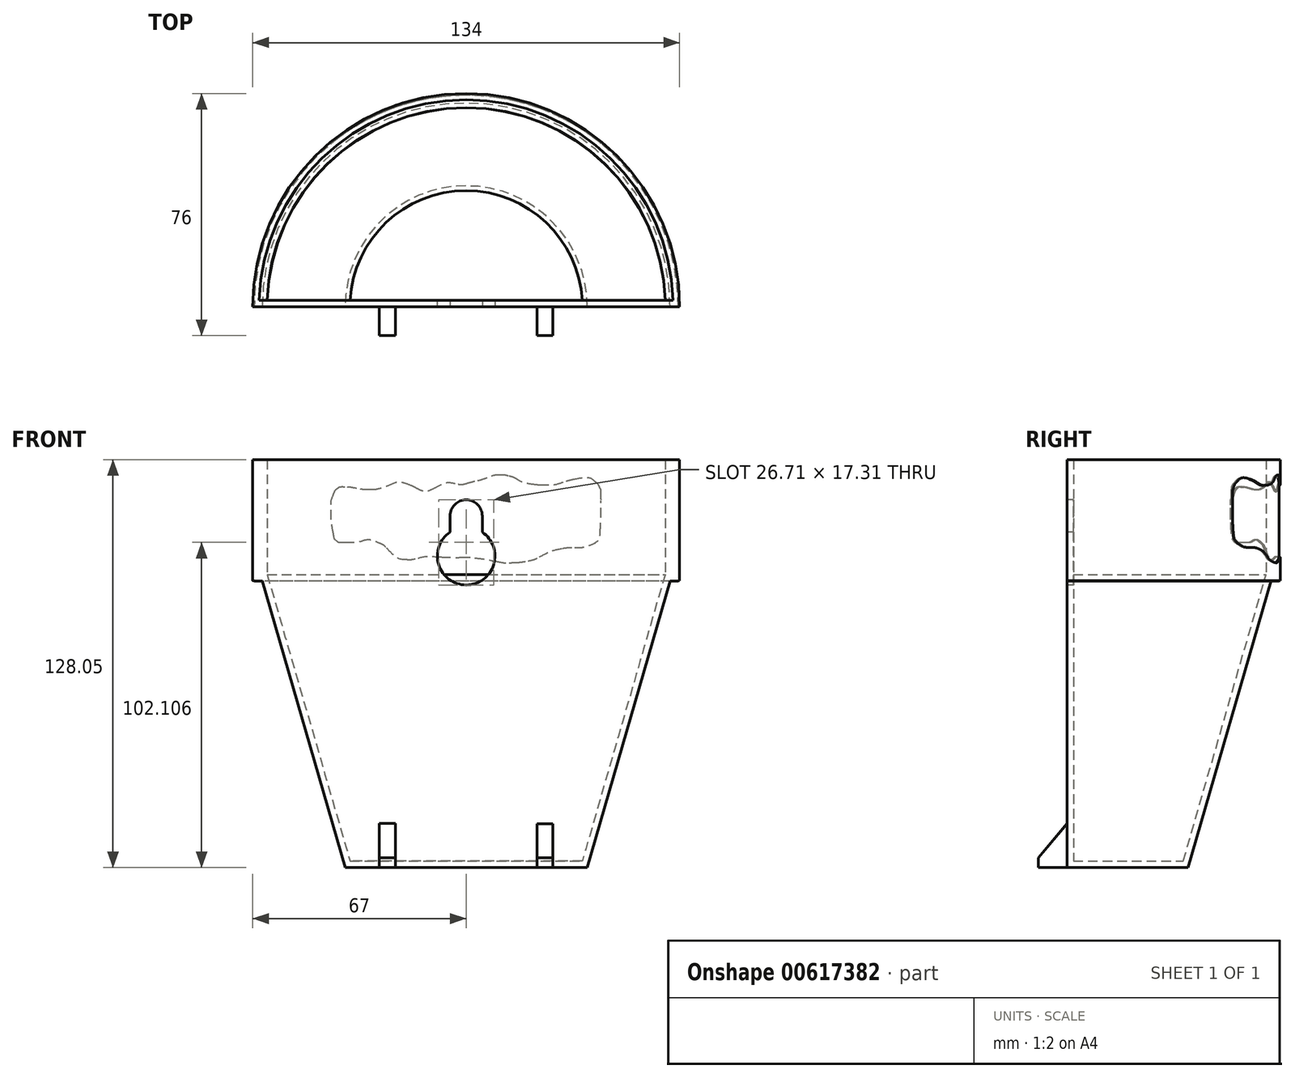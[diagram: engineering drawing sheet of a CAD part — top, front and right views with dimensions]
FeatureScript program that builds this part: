
annotation { "Feature Type Name" : "Feature", "Feature Type Description" : "" }
export const myFeature = defineFeature(function(context is Context, id is Id, definition is map)
    precondition{}
    {
        {
            var Q0;
            Q0=qCreatedBy(makeId("Front.planeOp"),FACE);
            var sketch = newSketch(context, id + "F0", { "sketchPlane" : qUnion([Q0])});
            skLineSegment(sketch, "E0", {"start": v(0, 56.42) * mm, "end": v(-67, 56.42) * mm});
            skLineSegment(sketch, "E1", {"start": v(-67, 56.42) * mm, "end": v(-67, 18.42) * mm});
            skLineSegment(sketch, "E2", {"start": v(0, -71.58) * mm, "end": v(-38, -71.58) * mm});
            skLineSegment(sketch, "E3", {"start": v(-67, 18.42) * mm, "end": v(-64, 18.42) * mm});
            skLineSegment(sketch, "E4", {"start": v(0, 56.42) * mm, "end": v(0, -71.58) * mm});
            skLineSegment(sketch, "E5", {"start": v(-64, 18.42) * mm, "end": v(-38, -71.58) * mm});
            skLineSegment(sketch, "E6.MirrorCS", {"start": v(0, 56.42) * mm, "end": v(67, 56.42) * mm});
            skLineSegment(sketch, "E7.MirrorCS", {"start": v(67, 56.42) * mm, "end": v(67, 18.42) * mm});
            skLineSegment(sketch, "E8.MirrorCS", {"start": v(67, 18.42) * mm, "end": v(64, 18.42) * mm});
            skLineSegment(sketch, "E9.MirrorCS", {"start": v(64, 18.42) * mm, "end": v(38, -71.58) * mm});
            skLineSegment(sketch, "E10.MirrorCS", {"start": v(0, -71.58) * mm, "end": v(38, -71.58) * mm});
            skSolve(sketch);
        }
        {
            var Q0;
            {var subQ0=sQuery(id+"F0.wireOp",EDGE,"E3");Q0=makeQuery(id+"F0.imprint","IMPRINT",FACE,{"disambiguationData":[TD([[makeQuery(id+"F0.imprint","IMPRINT",EDGE,{"derivedFrom":subQ0}),1.0]])]});}
            var Q1;
            {var subQ1=sQuery(id+"F0.wireOp",EDGE,"E0");Q1=makeQuery(id+"F0.imprint","IMPRINT",FACE,{"disambiguationData":[TD([[makeQuery(id+"F0.imprint","IMPRINT",EDGE,{"derivedFrom":subQ1}),1.0]])]});}
            var Q2;
            Q2=makeQuery(id+"F0.imprint","IMPRINT",FACE,{"disambiguationData":[TD([[makeQuery(id+"F0.imprint","IMPRINT",EDGE,{"derivedFrom":sQuery(id+"F0.wireOp",EDGE,"Kfnrekvc-ZjTY-c2iQ-cK4z-hKnBe4uEAVNk")}),1.0]])]});
            var Q3;
            Q3=sQuery(id+"F0.wireOp",EDGE,"E4");
            revolve(context, id + "F1", {"entities" : qUnion([Q0, Q1, Q2]), "axis" : qUnion([Q3]), "revolveType" : RevolveType.ONE_DIRECTION, "angle" : 180 * degree});
        }
        {
            var Q0;
            Q0=makeQuery(id+"FK2OT3XlAi37Aaq_1.splitOp","SPLIT",FACE,{"derivedFrom":makeQuery(id+"F1.opRevolve","SWEPT_FACE",FACE,{"disambiguationData":[OSD([sQuery(id+"F0.wireOp",EDGE,"E0")])]}),"isFromBackBody":true});
            shell(context, id + "F2", {"entities" : qUnion([Q0]), "thickness" : 2 * mm});
        }
        {
            var Q0;
            Q0=qCreatedBy(makeId("Front.planeOp"),FACE);
            var sketch = newSketch(context, id + "F3", { "sketchPlane" : qUnion([Q0])});
            skPoint(sketch, "E11.middle", {"position": v(0, -64.08) * mm});
            skLineSegment(sketch, "E12.bottom", {"start": v(-27.21, -56.57) * mm, "end": v(-22.21, -56.57) * mm});
            skLineSegment(sketch, "E12.top", {"start": v(-27.21, -71.57) * mm, "end": v(-22.21, -71.57) * mm});
            skLineSegment(sketch, "E12.left", {"start": v(-27.21, -56.57) * mm, "end": v(-27.21, -71.57) * mm});
            skLineSegment(sketch, "E12.right", {"start": v(-22.21, -56.57) * mm, "end": v(-22.21, -71.57) * mm});
            skPoint(sketch, "E12.middle", {"position": v(-24.71, -64.07) * mm});
            skLineSegment(sketch, "E13.bottom", {"start": v(22.21, -56.63) * mm, "end": v(27.21, -56.63) * mm});
            skLineSegment(sketch, "E13.top", {"start": v(22.21, -71.63) * mm, "end": v(27.21, -71.63) * mm});
            skLineSegment(sketch, "E13.left", {"start": v(22.21, -56.63) * mm, "end": v(22.21, -71.63) * mm});
            skLineSegment(sketch, "E13.right", {"start": v(27.21, -56.63) * mm, "end": v(27.21, -71.63) * mm});
            skPoint(sketch, "E13.middle", {"position": v(24.71, -64.13) * mm});
            skLineSegment(sketch, "E14", {"start": v(0, -71.68) * mm, "end": v(-22.21, -71.57) * mm, "construction": true});
            skLineSegment(sketch, "E15", {"start": v(0, -71.68) * mm, "end": v(22.21, -71.63) * mm, "construction": true});
            skSolve(sketch);
        }
        {
            var Q0;
            Q0=qSketchRegion(id+"F3",true);
            extrude(context, id + "F4", {"entities" : qUnion([Q0]), "operationType" : NewBodyOperationType.ADD, "depth" : 9 * mm});
        }
        {
            var Q0;
            Q0=qCreatedBy(makeId("Front.planeOp"),FACE);
            var sketch = newSketch(context, id + "F5", { "sketchPlane" : qUnion([Q0])});
            skCircle(sketch, "E16", {"center": v(0, 26.17) * mm, "radius": 9.05 * mm});
            skArc(sketch, "E17", {"start": v(5.05, 38.78) * mm, "mid": v(0.02, 43.83) * mm, "end": v(-5.05, 38.81) * mm});
            skLineSegment(sketch, "E18", {"start": v(-5.05, 38.81) * mm, "end": v(-5.05, 33.68) * mm});
            skLineSegment(sketch, "E19", {"start": v(5.05, 38.78) * mm, "end": v(5.05, 33.68) * mm});
            skSolve(sketch);
        }
        {
            var Q0;
            {var subQ0=sQuery(id+"F5.wireOp",EDGE,"E16");var subQ1=sQuery(id+"F5.wireOp",EDGE,"mXHq6PA0-CqQh-Lv1D-GdnR-uttjTBgCqYAd");var subQ2=makeQuery(id+"F5.imprint","INTERSECT",VERTEX,{"disambiguationData":[OD(0.0)],"derivedFrom":[subQ1,subQ0]});Q0=makeQuery(id+"F5.imprint","IMPRINT",FACE,{"disambiguationData":[TD([[makeQuery(id+"F5.imprint","IMPRINT",EDGE,{"disambiguationData":[TD([[subQ2,1.0]])],"derivedFrom":subQ1}),1.0]])]});}
            var Q1;
            {var subQ0=sQuery(id+"F5.wireOp",EDGE,"E16");var subQ1=sQuery(id+"F5.wireOp",EDGE,"mXHq6PA0-CqQh-Lv1D-GdnR-uttjTBgCqYAd");var subQ2=makeQuery(id+"F5.imprint","INTERSECT",VERTEX,{"disambiguationData":[OD(0.0)],"derivedFrom":[subQ1,subQ0]});Q1=makeQuery(id+"F5.imprint","IMPRINT",FACE,{"disambiguationData":[TD([[makeQuery(id+"F5.imprint","IMPRINT",EDGE,{"disambiguationData":[TD([[subQ2,-1.0]])],"derivedFrom":subQ1}),-1.0]])]});}
            var Q2;
            {var subQ0=sQuery(id+"F5.wireOp",EDGE,"E16");var subQ1=sQuery(id+"F5.wireOp",EDGE,"mXHq6PA0-CqQh-Lv1D-GdnR-uttjTBgCqYAd");var subQ2=makeQuery(id+"F5.imprint","INTERSECT",VERTEX,{"disambiguationData":[OD(0.0)],"derivedFrom":[subQ1,subQ0]});Q2=makeQuery(id+"F5.imprint","IMPRINT",FACE,{"disambiguationData":[TD([[makeQuery(id+"F5.imprint","IMPRINT",EDGE,{"disambiguationData":[TD([[subQ2,-1.0]])],"derivedFrom":subQ1}),1.0]])]});}
            var Q3;
            Q3=makeQuery(id+"F5.imprint","IMPRINT",FACE,{"disambiguationData":[TD([[makeQuery(id+"F5.imprint","IMPRINT",EDGE,{"derivedFrom":sQuery(id+"F5.wireOp",EDGE,"E17")}),1.0]])]});
            var Q4;
            {var subQ0=sQuery(id+"F5.wireOp",EDGE,"E16");var subQ1=makeQuery(id+"F5.imprint","INTERSECT",VERTEX,{"derivedFrom":[subQ0,sQuery(id+"F5.wireOp",EDGE,"E18")]});Q4=makeQuery(id+"F5.imprint","IMPRINT",FACE,{"disambiguationData":[TD([[makeQuery(id+"F5.imprint","IMPRINT",EDGE,{"disambiguationData":[TD([[subQ1,1.0]])],"derivedFrom":subQ0}),1.0]])]});}
            var Q5;
            Q5=sQuery(id+"F5.wireOp",EDGE,"mXHq6PA0-CqQh-Lv1D-GdnR-uttjTBgCqYAd");
            var Q6;
            Q6=sQuery(id+"F5.wireOp",EDGE,"E16");
            extrude(context, id + "F6", {"entities" : qUnion([Q0, Q1, Q2, Q3, Q4]), "operationType" : NewBodyOperationType.REMOVE, "surfaceEntities" : qUnion([Q5, Q6]), "oppositeDirection" : true, "depth" : 10 * mm, "offsetDistance" : 25 * mm});
        }
        {
            var Q0;
            Q0=makeQuery(id+"F4.opExtrude","CAP_EDGE",EDGE,{"disambiguationData":[OSD([sQuery(id+"F3.wireOp",EDGE,"E11.bottom")])],"isStart":false});
            var Q1;
            Q1=makeQuery(id+"F4.opExtrude","CAP_EDGE",EDGE,{"disambiguationData":[OSD([sQuery(id+"F3.wireOp",EDGE,"E12.bottom")])],"isStart":false});
            var Q2;
            Q2=makeQuery(id+"F4.opExtrude","CAP_EDGE",EDGE,{"disambiguationData":[OSD([sQuery(id+"F3.wireOp",EDGE,"E13.bottom")])],"isStart":false});
            chamfer(context, id + "F7", {"entities" : qUnion([Q0, Q1, Q2]), "chamferType" : ChamferType.OFFSET_ANGLE, "width" : 10 * mm, "oppositeDirection" : false, "angle" : 50 * degree, "tangentPropagation" : true});
        }
        {
            var Q0;
            Q0=makeQuery(id+"F2.opShell","OFFSET_FACE",FACE,{"disambiguationData":[OSD([sQuery(id+"F0.wireOp",EDGE,"E0"),sQuery(id+"F0.wireOp",EDGE,"E1"),sQuery(id+"F0.wireOp",EDGE,"E2"),sQuery(id+"F0.wireOp",EDGE,"E3"),sQuery(id+"F0.wireOp",EDGE,"E4"),sQuery(id+"F0.wireOp",EDGE,"E5")])]});
            cPlane(context, id + "F8", {"entities" : qUnion([Q0]), "cplaneType" : CPlaneType.OFFSET, "offset" : 66.8 * mm, "width" : 150 * mm, "height" : 150 * mm});
        }
        {
            var Q0;
            Q0=makeQuery(id+"F1.opRevolve","SWEPT_FACE",FACE,{"disambiguationData":[OSD([sQuery(id+"F0.wireOp",EDGE,"E0")])]});
            var sketch = newSketch(context, id + "F9", { "sketchPlane" : qUnion([Q0])});
            skCircle(sketch, "E20", {"center": v(0, 0) * mm, "radius": 67.75 * mm});
            skCircle(sketch, "E21", {"center": v(0, 0) * mm, "radius": 91 * mm});
            skSolve(sketch);
        }
        {
            var Q0;
            Q0=qSketchRegion(id+"F9",true);
            extrude(context, id + "F10", {"entities" : qUnion([Q0]), "operationType" : NewBodyOperationType.REMOVE, "oppositeDirection" : true, "depth" : 124 * mm});
        }
        {
            var Q0;
            Q0=qCreatedBy(id+"F8.planeOp",FACE);
            var sketch = newSketch(context, id + "F11", { "sketchPlane" : qUnion([Q0])});
            skFitSpline(sketch, "E22", {"points": [v(-14.21, 60.71) * mm, v(-15.23, 60.8) * mm, v(-17.15, 61.07) * mm, v(-17.98, 61.24) * mm]});
            skFitSpline(sketch, "E23", {"points": [v(-17.98, 61.24) * mm, v(-19.27, 61.5) * mm, v(-20.2, 61.84) * mm, v(-21.41, 62.47) * mm]});
            skFitSpline(sketch, "E24", {"points": [v(-21.41, 62.47) * mm, v(-24.2, 63.93) * mm, v(-26.13, 64.66) * mm, v(-28.48, 65.15) * mm]});
            skFitSpline(sketch, "E25", {"points": [v(-28.48, 65.15) * mm, v(-29.29, 65.32) * mm, v(-30, 65.37) * mm, v(-32.2, 65.43) * mm]});
            skFitSpline(sketch, "E26", {"points": [v(-32.2, 65.43) * mm, v(-35.22, 65.52) * mm, v(-35.76, 65.6) * mm, v(-36.93, 66.16) * mm]});
            skFitSpline(sketch, "E27", {"points": [v(-36.93, 66.16) * mm, v(-38.77, 67.04) * mm, v(-39.83, 68.44) * mm, v(-40.02, 70.25) * mm]});
            skFitSpline(sketch, "E28", {"points": [v(-40.02, 70.25) * mm, v(-40.16, 71.57) * mm, v(-40.28, 76.7) * mm, v(-40.26, 80.14) * mm]});
            skFitSpline(sketch, "E29", {"points": [v(-39.96, 84.14) * mm, v(-39.6, 85.02) * mm, v(-39.23, 85.55) * mm, v(-38.6, 86.04) * mm]});
            skFitSpline(sketch, "E30", {"points": [v(-38.6, 86.04) * mm, v(-37.32, 87.06) * mm, v(-35.24, 87.34) * mm, v(-32.5, 86.87) * mm]});
            skFitSpline(sketch, "E31", {"points": [v(-32.5, 86.87) * mm, v(-31.47, 86.7) * mm, v(-30.34, 86.4) * mm, v(-28.67, 85.86) * mm]});
            skFitSpline(sketch, "E32", {"points": [v(-28.67, 85.86) * mm, v(-26.48, 85.16) * mm, v(-25.24, 84.96) * mm, v(-23.15, 84.96) * mm]});
            skFitSpline(sketch, "E33", {"points": [v(-23.15, 84.96) * mm, v(-22.35, 84.96) * mm, v(-21.18, 85.03) * mm, v(-20.54, 85.12) * mm]});
            skFitSpline(sketch, "E34", {"points": [v(-20.54, 85.12) * mm, v(-18.34, 85.42) * mm, v(-15.77, 86.13) * mm, v(-14.88, 86.67) * mm]});
            skFitSpline(sketch, "E35", {"points": [v(-14.88, 86.67) * mm, v(-14.07, 87.17) * mm, v(-12.87, 87.67) * mm, v(-11.9, 87.91) * mm]});
            skFitSpline(sketch, "E36", {"points": [v(-11.9, 87.91) * mm, v(-11.18, 88.1) * mm, v(-10.77, 88.13) * mm, v(-9.58, 88.13) * mm]});
            skFitSpline(sketch, "E37", {"points": [v(-9.58, 88.13) * mm, v(-7.91, 88.13) * mm, v(-7.18, 87.99) * mm, v(-5.29, 87.27) * mm]});
            skFitSpline(sketch, "E38", {"points": [v(-5.29, 87.27) * mm, v(-3.99, 86.78) * mm, v(-2.9, 86.45) * mm, v(-1.6, 86.14) * mm]});
            skFitSpline(sketch, "E39", {"points": [v(-1.6, 86.14) * mm, v(-1.1, 86.03) * mm, v(-0.13, 85.78) * mm, v(0.55, 85.59) * mm]});
            skFitSpline(sketch, "E40", {"points": [v(0.55, 85.59) * mm, v(2.03, 85.17) * mm, v(2.79, 85.14) * mm, v(4.3, 85.4) * mm]});
            skFitSpline(sketch, "E41", {"points": [v(4.3, 85.4) * mm, v(6.34, 85.76) * mm, v(7.65, 85.52) * mm, v(10.1, 84.34) * mm]});
            skFitSpline(sketch, "E42", {"points": [v(10.1, 84.34) * mm, v(12.42, 83.22) * mm, v(13.55, 82.94) * mm, v(14.56, 83.25) * mm]});
            skFitSpline(sketch, "E43", {"points": [v(14.56, 83.25) * mm, v(14.85, 83.34) * mm, v(15.6, 83.69) * mm, v(16.21, 84.03) * mm]});
            skFitSpline(sketch, "E44", {"points": [v(16.21, 84.03) * mm, v(16.83, 84.37) * mm, v(17.63, 84.77) * mm, v(17.97, 84.9) * mm]});
            skFitSpline(sketch, "E45", {"points": [v(17.97, 84.9) * mm, v(19, 85.32) * mm, v(21.27, 85.96) * mm, v(22.8, 85.75) * mm]});
            skFitSpline(sketch, "E46", {"points": [v(22.8, 85.75) * mm, v(25.09, 84.74) * mm, v(26.57, 84.16) * mm, v(27.89, 83.82) * mm]});
            skFitSpline(sketch, "E47", {"points": [v(27.89, 83.82) * mm, v(28.82, 83.6) * mm, v(29.1, 83.56) * mm, v(30.58, 83.57) * mm]});
            skFitSpline(sketch, "E48", {"points": [v(30.58, 83.57) * mm, v(32.1, 83.57) * mm, v(32.41, 83.6) * mm, v(34.6, 84) * mm]});
            skFitSpline(sketch, "E49", {"points": [v(34.6, 84) * mm, v(36.58, 84.35) * mm, v(37.14, 84.42) * mm, v(38.19, 84.42) * mm]});
            skFitSpline(sketch, "E50", {"points": [v(38.19, 84.42) * mm, v(39.58, 84.42) * mm, v(39.98, 84.31) * mm, v(40.62, 83.8) * mm]});
            skFitSpline(sketch, "E51", {"points": [v(40.62, 83.8) * mm, v(41.14, 83.38) * mm, v(41.5, 82.8) * mm, v(41.88, 81.74) * mm]});
            skFitSpline(sketch, "E52", {"points": [v(41.88, 81.74) * mm, v(42.44, 80.2) * mm, v(42.49, 79.85) * mm, v(42.49, 77.2) * mm]});
            skFitSpline(sketch, "E53", {"points": [v(42.49, 77.2) * mm, v(42.48, 74.69) * mm, v(42.34, 72.96) * mm, v(41.92, 70.56) * mm]});
            skFitSpline(sketch, "E54", {"points": [v(41.92, 70.56) * mm, v(41.56, 68.48) * mm, v(41.46, 68.19) * mm, v(40.86, 67.68) * mm]});
            skFitSpline(sketch, "E55", {"points": [v(40.86, 67.68) * mm, v(40.27, 67.18) * mm, v(39.77, 67.05) * mm, v(38.23, 67.05) * mm]});
            skFitSpline(sketch, "E56", {"points": [v(38.23, 67.05) * mm, v(35.56, 67.04) * mm, v(34.05, 67.16) * mm, v(33.1, 67.44) * mm]});
            skFitSpline(sketch, "E57", {"points": [v(33.1, 67.44) * mm, v(31.4, 67.95) * mm, v(30.14, 67.86) * mm, v(28.22, 67.1) * mm]});
            skFitSpline(sketch, "E58", {"points": [v(28.22, 67.1) * mm, v(26.75, 66.51) * mm, v(26.28, 66.21) * mm, v(25.37, 65.28) * mm]});
            skFitSpline(sketch, "E59", {"points": [v(25.37, 65.28) * mm, v(23.19, 63.06) * mm, v(21.33, 61.94) * mm, v(19.52, 61.74) * mm]});
            skFitSpline(sketch, "E60", {"points": [v(19.52, 61.74) * mm, v(18.5, 61.63) * mm, v(17.41, 61.74) * mm, v(15.77, 62.11) * mm]});
            skFitSpline(sketch, "E61", {"points": [v(15.77, 62.11) * mm, v(13.66, 62.6) * mm, v(12.37, 62.66) * mm, v(8.71, 62.47) * mm]});
            skFitSpline(sketch, "E62", {"points": [v(8.71, 62.47) * mm, v(6.82, 62.37) * mm, v(4.44, 62.32) * mm, v(2.66, 62.33) * mm]});
            skFitSpline(sketch, "E63", {"points": [v(2.66, 62.33) * mm, v(0.28, 62.35) * mm, v(-0.53, 62.32) * mm, v(-1.6, 62.18) * mm]});
            skFitSpline(sketch, "E64", {"points": [v(-1.6, 62.18) * mm, v(-3.69, 61.9) * mm, v(-5.8, 61.56) * mm, v(-8.26, 61.08) * mm]});
            skFitSpline(sketch, "E65", {"points": [v(-8.26, 61.08) * mm, v(-10.46, 60.66) * mm, v(-10.6, 60.65) * mm, v(-12.2, 60.67) * mm]});
            skFitSpline(sketch, "E66", {"points": [v(-12.2, 60.67) * mm, v(-13.1, 60.68) * mm, v(-14, 60.7) * mm, v(-14.21, 60.71) * mm]});
            skLineSegment(sketch, "E67", {"start": v(-40.26, 80.14) * mm, "end": v(-40.23, 83.46) * mm});
            skLineSegment(sketch, "E68", {"start": v(-40.23, 83.46) * mm, "end": v(-39.96, 84.14) * mm});
            skLineSegment(sketch, "E69", {"start": v(-39.96, 84.14) * mm, "end": v(-40.26, 80.14) * mm});
            skFitSpline(sketch, "E70", {"points": [v(-15.59, 24.15) * mm, v(-16.63, 24.24) * mm, v(-18.6, 24.5) * mm, v(-19.44, 24.68) * mm]});
            skFitSpline(sketch, "E71", {"points": [v(-19.44, 24.68) * mm, v(-20.76, 24.94) * mm, v(-21.72, 25.28) * mm, v(-22.96, 25.91) * mm]});
            skFitSpline(sketch, "E72", {"points": [v(-22.96, 25.91) * mm, v(-25.81, 27.37) * mm, v(-27.79, 28.1) * mm, v(-30.2, 28.6) * mm]});
            skFitSpline(sketch, "E73", {"points": [v(-30.2, 28.6) * mm, v(-31.02, 28.76) * mm, v(-31.76, 28.81) * mm, v(-34.01, 28.87) * mm]});
            skFitSpline(sketch, "E74", {"points": [v(-34.01, 28.87) * mm, v(-37.1, 28.96) * mm, v(-37.65, 29.04) * mm, v(-38.85, 29.6) * mm]});
            skFitSpline(sketch, "E75", {"points": [v(-38.85, 29.6) * mm, v(-40.73, 30.48) * mm, v(-41.82, 31.88) * mm, v(-42.02, 33.69) * mm]});
            skFitSpline(sketch, "E76", {"points": [v(-42.02, 33.69) * mm, v(-42.16, 35) * mm, v(-42.29, 40.13) * mm, v(-42.26, 43.57) * mm]});
            skFitSpline(sketch, "E77", {"points": [v(-41.95, 47.57) * mm, v(-41.59, 48.46) * mm, v(-41.2, 48.98) * mm, v(-40.57, 49.47) * mm]});
            skFitSpline(sketch, "E78", {"points": [v(-40.57, 49.47) * mm, v(-39.25, 50.5) * mm, v(-37.12, 50.77) * mm, v(-34.3, 50.3) * mm]});
            skFitSpline(sketch, "E79", {"points": [v(-34.3, 50.3) * mm, v(-33.26, 50.13) * mm, v(-32.1, 49.83) * mm, v(-30.4, 49.3) * mm]});
            skFitSpline(sketch, "E80", {"points": [v(-30.4, 49.3) * mm, v(-28.15, 48.6) * mm, v(-26.88, 48.4) * mm, v(-24.74, 48.4) * mm]});
            skFitSpline(sketch, "E81", {"points": [v(-24.74, 48.4) * mm, v(-23.91, 48.4) * mm, v(-22.72, 48.47) * mm, v(-22.06, 48.56) * mm]});
            skFitSpline(sketch, "E82", {"points": [v(-22.06, 48.56) * mm, v(-19.81, 48.86) * mm, v(-17.18, 49.56) * mm, v(-16.26, 50.1) * mm]});
            skFitSpline(sketch, "E83", {"points": [v(-16.26, 50.1) * mm, v(-15.44, 50.6) * mm, v(-14.2, 51.1) * mm, v(-13.21, 51.35) * mm]});
            skFitSpline(sketch, "E84", {"points": [v(-13.21, 51.35) * mm, v(-12.48, 51.53) * mm, v(-12.06, 51.57) * mm, v(-10.84, 51.57) * mm]});
            skFitSpline(sketch, "E85", {"points": [v(-10.84, 51.57) * mm, v(-9.13, 51.57) * mm, v(-8.38, 51.42) * mm, v(-6.44, 50.7) * mm]});
            skFitSpline(sketch, "E86", {"points": [v(-6.44, 50.7) * mm, v(-5.11, 50.21) * mm, v(-4, 49.88) * mm, v(-2.67, 49.58) * mm]});
            skFitSpline(sketch, "E87", {"points": [v(-2.67, 49.58) * mm, v(-2.15, 49.46) * mm, v(-1.16, 49.21) * mm, v(-0.46, 49.02) * mm]});
            skFitSpline(sketch, "E88", {"points": [v(-0.46, 49.02) * mm, v(1.05, 48.61) * mm, v(1.82, 48.57) * mm, v(3.38, 48.84) * mm]});
            skFitSpline(sketch, "E89", {"points": [v(3.38, 48.84) * mm, v(5.46, 49.2) * mm, v(6.8, 48.96) * mm, v(9.3, 47.78) * mm]});
            skFitSpline(sketch, "E90", {"points": [v(9.3, 47.78) * mm, v(11.69, 46.66) * mm, v(12.85, 46.38) * mm, v(13.88, 46.69) * mm]});
            skFitSpline(sketch, "E91", {"points": [v(13.88, 46.69) * mm, v(14.18, 46.77) * mm, v(14.94, 47.12) * mm, v(15.57, 47.47) * mm]});
            skFitSpline(sketch, "E92", {"points": [v(15.57, 47.47) * mm, v(16.21, 47.8) * mm, v(17.02, 48.2) * mm, v(17.38, 48.34) * mm]});
            skFitSpline(sketch, "E93", {"points": [v(17.38, 48.34) * mm, v(18.43, 48.76) * mm, v(20.75, 49.4) * mm, v(22.33, 49.19) * mm]});
            skFitSpline(sketch, "E94", {"points": [v(22.33, 49.19) * mm, v(24.66, 48.17) * mm, v(26.18, 47.6) * mm, v(27.53, 47.26) * mm]});
            skFitSpline(sketch, "E95", {"points": [v(27.53, 47.26) * mm, v(28.48, 47.03) * mm, v(28.77, 47) * mm, v(30.29, 47) * mm]});
            skFitSpline(sketch, "E96", {"points": [v(30.29, 47) * mm, v(31.85, 47) * mm, v(32.17, 47.04) * mm, v(34.4, 47.43) * mm]});
            skFitSpline(sketch, "E97", {"points": [v(34.4, 47.43) * mm, v(36.44, 47.79) * mm, v(37, 47.85) * mm, v(38.08, 47.85) * mm]});
            skFitSpline(sketch, "E98", {"points": [v(38.08, 47.85) * mm, v(39.5, 47.85) * mm, v(39.91, 47.75) * mm, v(40.57, 47.23) * mm]});
            skFitSpline(sketch, "E99", {"points": [v(40.57, 47.23) * mm, v(41.1, 46.81) * mm, v(41.47, 46.23) * mm, v(41.86, 45.17) * mm]});
            skFitSpline(sketch, "E100", {"points": [v(41.86, 45.17) * mm, v(42.44, 43.64) * mm, v(42.49, 43.29) * mm, v(42.48, 40.64) * mm]});
            skFitSpline(sketch, "E101", {"points": [v(42.48, 40.64) * mm, v(42.48, 38.12) * mm, v(42.33, 36.4) * mm, v(41.9, 34) * mm]});
            skFitSpline(sketch, "E102", {"points": [v(41.9, 34) * mm, v(41.54, 31.92) * mm, v(41.43, 31.63) * mm, v(40.82, 31.12) * mm]});
            skFitSpline(sketch, "E103", {"points": [v(40.82, 31.12) * mm, v(40.22, 30.61) * mm, v(39.7, 30.5) * mm, v(38.12, 30.49) * mm]});
            skFitSpline(sketch, "E104", {"points": [v(38.12, 30.49) * mm, v(35.4, 30.48) * mm, v(33.85, 30.6) * mm, v(32.87, 30.88) * mm]});
            skFitSpline(sketch, "E105", {"points": [v(32.87, 30.88) * mm, v(31.13, 31.39) * mm, v(29.84, 31.3) * mm, v(27.87, 30.53) * mm]});
            skFitSpline(sketch, "E106", {"points": [v(27.87, 30.53) * mm, v(26.37, 29.95) * mm, v(25.89, 29.65) * mm, v(24.95, 28.72) * mm]});
            skFitSpline(sketch, "E107", {"points": [v(24.95, 28.72) * mm, v(22.72, 26.5) * mm, v(20.82, 25.38) * mm, v(18.96, 25.18) * mm]});
            skFitSpline(sketch, "E108", {"points": [v(18.96, 25.18) * mm, v(17.91, 25.07) * mm, v(16.8, 25.18) * mm, v(15.12, 25.55) * mm]});
            skFitSpline(sketch, "E109", {"points": [v(15.12, 25.55) * mm, v(12.96, 26.03) * mm, v(11.64, 26.1) * mm, v(7.9, 25.9) * mm]});
            skFitSpline(sketch, "E110", {"points": [v(7.9, 25.9) * mm, v(5.96, 25.8) * mm, v(3.52, 25.75) * mm, v(1.7, 25.77) * mm]});
            skFitSpline(sketch, "E111", {"points": [v(1.7, 25.77) * mm, v(-0.74, 25.79) * mm, v(-1.57, 25.76) * mm, v(-2.67, 25.62) * mm]});
            skFitSpline(sketch, "E112", {"points": [v(-2.67, 25.62) * mm, v(-4.8, 25.34) * mm, v(-6.97, 25) * mm, v(-9.5, 24.52) * mm]});
            skFitSpline(sketch, "E113", {"points": [v(-9.5, 24.52) * mm, v(-11.74, 24.1) * mm, v(-11.88, 24.09) * mm, v(-13.52, 24.1) * mm]});
            skFitSpline(sketch, "E114", {"points": [v(-13.52, 24.1) * mm, v(-14.45, 24.11) * mm, v(-15.38, 24.14) * mm, v(-15.59, 24.15) * mm]});
            skLineSegment(sketch, "E115", {"start": v(-42.26, 43.57) * mm, "end": v(-42.23, 46.9) * mm});
            skLineSegment(sketch, "E116", {"start": v(-42.23, 46.9) * mm, "end": v(-41.95, 47.57) * mm});
            skLineSegment(sketch, "E117", {"start": v(-41.95, 47.57) * mm, "end": v(-42.26, 43.57) * mm});
            skSolve(sketch);
        }
        {
            var Q0;
            Q0 = qSketchRegion(id + "F11", true);
            extrude(context, id + "F12", {"entities" : qUnion([Q0]), "operationType" : NewBodyOperationType.REMOVE, "oppositeDirection" : true, "depth" : 30 * mm, "offsetDistance" : 25 * mm});
        }
        {
            var Q0;
            Q0=qCreatedBy(makeId("Front.planeOp"),FACE);
            var sketch = newSketch(context, id + "F13", { "sketchPlane" : qUnion([Q0])});
            skLineSegment(sketch, "E118.bottom", {"start": v(66.54, 56.4) * mm, "end": v(62.54, 56.4) * mm});
            skLineSegment(sketch, "E118.top", {"start": v(66.54, 18.4) * mm, "end": v(62.54, 18.4) * mm});
            skLineSegment(sketch, "E118.left", {"start": v(66.54, 56.4) * mm, "end": v(66.54, 18.4) * mm});
            skLineSegment(sketch, "E118.right", {"start": v(62.54, 56.4) * mm, "end": v(62.54, 18.4) * mm});
            skSolve(sketch);
        }
        {
            var Q0;
            Q0 = qSketchRegion(id + "F13", true);
            var Q1;
            Q1=sQuery(id+"F0.wireOp",EDGE,"E4");
            revolve(context, id + "F14", {"operationType" : NewBodyOperationType.ADD, "entities" : qUnion([Q0]), "axis" : qUnion([Q1]), "revolveType" : RevolveType.ONE_DIRECTION, "oppositeDirection" : true, "angle" : 180 * degree});
        }
    });
